# Revit family: 1058xxx Enna Surface USB
name_source: partatom
category: Lighting Fixtures
revit_build: Autodesk Revit 2018 (Build: 20170223_1515(x64)
units: mm (PartAtom-declared; Revit-internal decimal feet)

## family parameters
Always vertical = Yes
Cut with Voids When Loaded = No
Host = Wall
Light Source = Yes
OmniClass Number = 23.80.70.00
OmniClass Title = Lighting
Part Type = Normal
Room Calculation Point = No
Round Connector Dimension = Use Diameter
Shared = No

## types (3) — shared parameters
Color Filter = 16777215
Dimming Lamp Color Temperature Shift = <None>
Driver Required = No
Manufacturer = Astro Lighting Ltd
Manufacturer URL - Europe and Rest of World = www.astrolighting.com
Manufacturer URL - North America = us.astrolighting.com
Tilt Angle = 60.00°
URL = www.astrolighting.com

## per-type parameters (varying)
| type | ADA compliant | Apparent Load | Dimmable | Driver Included | Efficacy (lm/w) | Electrical Class | Lamp | Light Source Fixed | Location / IP Rating | Main Finish | Main Material | Photometric Web File | Power (Watts) | Product CCT | Product CRI | Product Dimensions (MM) | Product Location | Product Name | Product SKU | Product Weight (KG) |
| CE | N / A | 0 VA |  |  |  | 1 |  |  |  |  | Metal - Steel | generic |  | 2700K / 3000K | 80 / 90 |  |  |  | 1234001 |  |
| ETL |  | 0 VA |  |  |  | 0 |  |  | DAMP |  | Metal - Steel | generic |  | 2700K / 3000K | 80 / 90 |  | Bathroom |  | 1234001 |  |
| 1058xxx Enna Surface USB | N / A | 11 VA | No | Yes (Integrated) | 36 | 1 | 2W Integrated LED | Yes | IP20 | Matt Black | Metal - Zinc | 1407002_Micro Recess Unswitched_Photometry_IES_Iss. 01.ies | 4.1W | 2700K | 90 | 225 x 80 x 144 | Wall | Enna Surface USB | 1058153 | 0.876 |

## geometry (parser evidence)
native form markers: Sweep x1
no freeform markers — native parametric forms only
